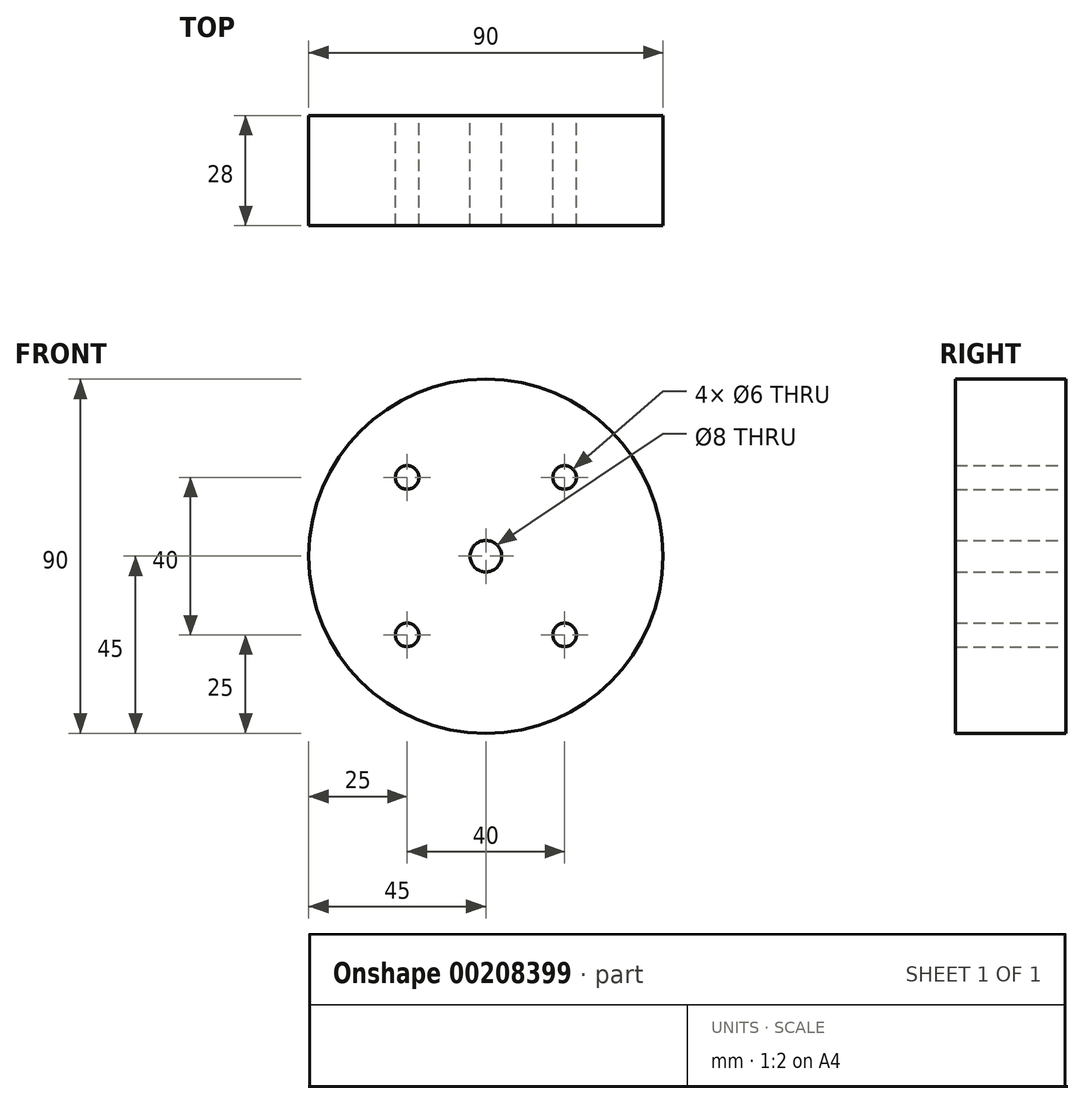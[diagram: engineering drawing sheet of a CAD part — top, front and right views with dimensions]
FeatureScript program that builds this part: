
annotation { "Feature Type Name" : "Feature", "Feature Type Description" : "" }
export const myFeature = defineFeature(function(context is Context, id is Id, definition is map)
    precondition{}
    {
        {
            var Q0;
            Q0=qCreatedBy(makeId("Front.planeOp"),FACE);
            var sketch = newSketch(context, id + "F0", { "sketchPlane" : qUnion([Q0])});
            skCircle(sketch, "E0", {"center": v(0, 0) * mm, "radius": 45 * mm});
            skCircle(sketch, "E1", {"center": v(0, 0) * mm, "radius": 4 * mm});
            skCircle(sketch, "E2", {"center": v(20, 20) * mm, "radius": 3 * mm});
            skCircle(sketch, "E3", {"center": v(-20, 20) * mm, "radius": 3 * mm});
            skCircle(sketch, "E4", {"center": v(20, -20) * mm, "radius": 3 * mm});
            skCircle(sketch, "E5", {"center": v(-20, -20) * mm, "radius": 3 * mm});
            skSolve(sketch);
        }
        {
            var Q0;
            Q0=makeQuery(id+"F0.imprint","IMPRINT",FACE,{"disambiguationData":[TD([[makeQuery(id+"F0.imprint","IMPRINT",EDGE,{"derivedFrom":sQuery(id+"F0.wireOp",EDGE,"E0")}),1.0]])]});
            extrude(context, id + "F1", {"entities" : qUnion([Q0]), "depth" : 28 * mm, "symmetric" : true});
        }
    });
